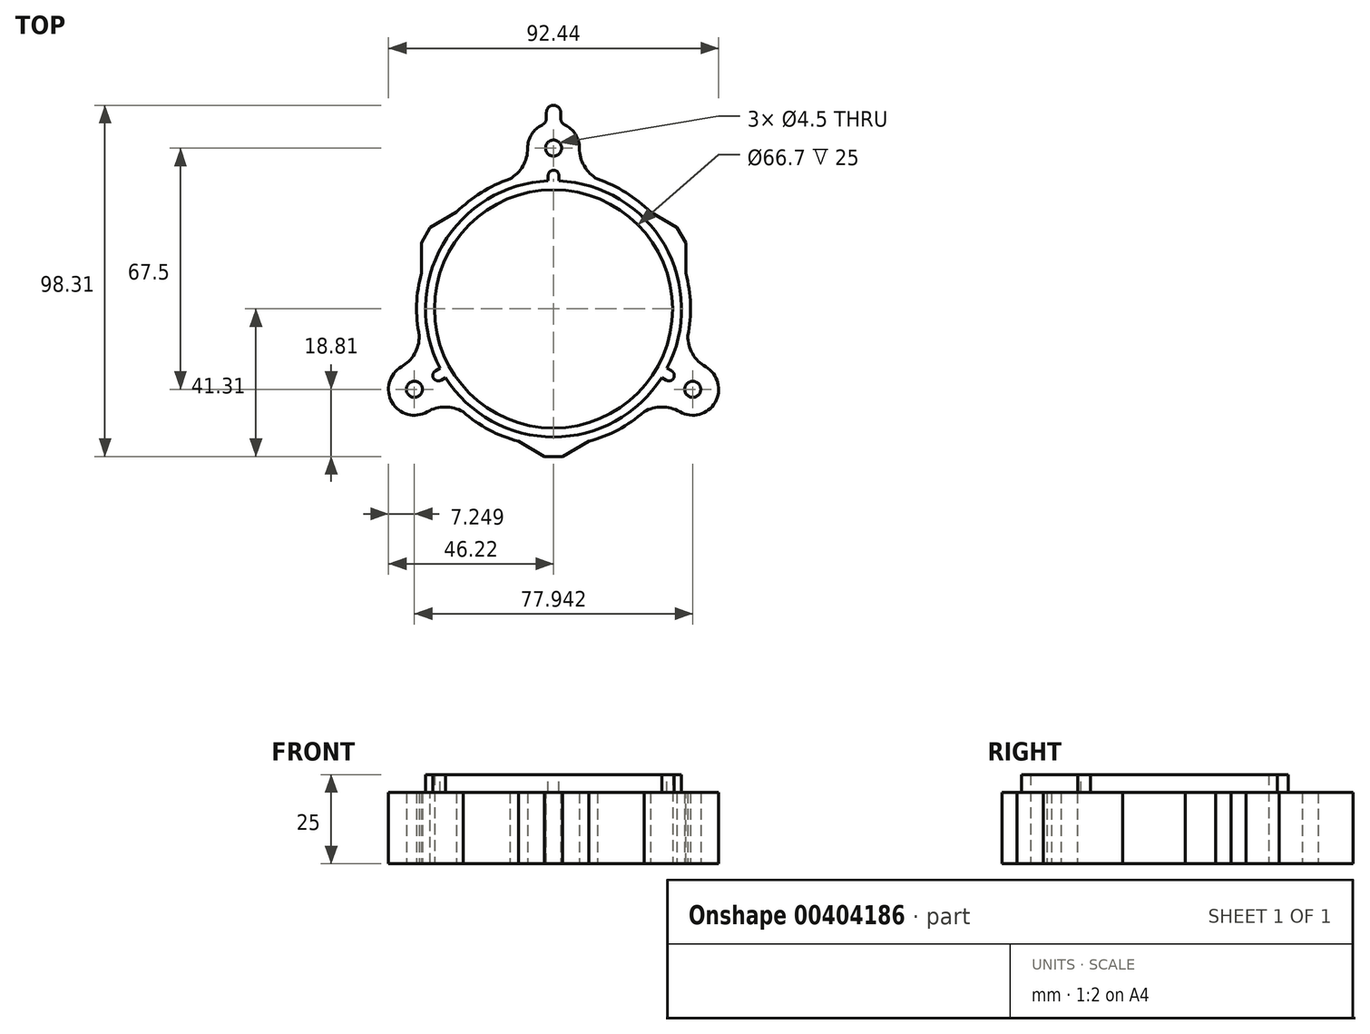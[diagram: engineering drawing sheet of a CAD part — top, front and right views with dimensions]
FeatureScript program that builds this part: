
annotation { "Feature Type Name" : "Feature", "Feature Type Description" : "" }
export const myFeature = defineFeature(function(context is Context, id is Id, definition is map)
    precondition{}
    {
        {
            var Q0;
            Q0=qCreatedBy(makeId("Top.planeOp"),FACE);
            var sketch = newSketch(context, id + "F0", { "sketchPlane" : qUnion([Q0])});
            skCircle(sketch, "E0", {"center": v(0, 0) * mm, "radius": 33.35 * mm});
            skCircle(sketch, "E1", {"center": v(0, 45) * mm, "radius": 2.25 * mm});
            skCircle(sketch, "E2", {"center": v(38.97, -22.5) * mm, "radius": 2.25 * mm});
            skCircle(sketch, "E3", {"center": v(-38.97, -22.5) * mm, "radius": 2.25 * mm});
            skArc(sketch, "E4", {"start": v(-25.35, -28.78) * mm, "mid": v(0, -38.35) * mm, "end": v(25.35, -28.78) * mm});
            skLineSegment(sketch, "E5", {"start": v(0, 0) * mm, "end": v(38.97, -22.5) * mm, "construction": true});
            skLineSegment(sketch, "E6", {"start": v(-38.97, -22.5) * mm, "end": v(0, 0) * mm, "construction": true});
            skArc(sketch, "E7", {"start": v(7.25, 45) * mm, "mid": v(5.8, 49.36) * mm, "end": v(2, 51.97) * mm});
            skArc(sketch, "E8.1.0", {"start": v(-42.6, -16.22) * mm, "mid": v(-45.25, -26.12) * mm, "end": v(-35.35, -28.78) * mm});
            skArc(sketch, "E8.2.0", {"start": v(35.35, -28.78) * mm, "mid": v(45.25, -26.12) * mm, "end": v(42.6, -16.22) * mm});
            skArc(sketch, "E9", {"start": v(-12.25, 36.34) * mm, "mid": v(-8.59, 40) * mm, "end": v(-7.25, 45) * mm});
            skArc(sketch, "E10.MirrorCS", {"start": v(12.25, 36.34) * mm, "mid": v(8.59, 40) * mm, "end": v(7.25, 45) * mm});
            skArc(sketch, "E11.1.0", {"start": v(-25.35, -28.78) * mm, "mid": v(-30.35, -27.44) * mm, "end": v(-35.35, -28.78) * mm});
            skArc(sketch, "E11.1.1", {"start": v(-37.6, -7.57) * mm, "mid": v(-38.94, -12.56) * mm, "end": v(-42.6, -16.22) * mm});
            skArc(sketch, "E11.2.0", {"start": v(37.6, -7.57) * mm, "mid": v(38.94, -12.56) * mm, "end": v(42.6, -16.22) * mm});
            skArc(sketch, "E11.2.1", {"start": v(25.35, -28.78) * mm, "mid": v(30.35, -27.44) * mm, "end": v(35.35, -28.78) * mm});
            skArc(sketch, "E12.trimOffspring", {"start": v(37.6, -7.57) * mm, "mid": v(33.21, 19.18) * mm, "end": v(12.25, 36.34) * mm});
            skArc(sketch, "E13.trimOffspring", {"start": v(-12.25, 36.34) * mm, "mid": v(-33.21, 19.17) * mm, "end": v(-37.6, -7.57) * mm});
            skLineSegment(sketch, "E14", {"start": v(-2, 54.13) * mm, "end": v(-2, 51.97) * mm});
            skArc(sketch, "E15", {"start": v(-2, 54.13) * mm, "mid": v(0, 60.5) * mm, "end": v(2, 54.13) * mm, "construction": true});
            skLineSegment(sketch, "E16.MirrorCS", {"start": v(2, 54.13) * mm, "end": v(2, 51.97) * mm});
            skArc(sketch, "E17.trimOffspring", {"start": v(-2, 51.97) * mm, "mid": v(-5.8, 49.36) * mm, "end": v(-7.25, 45) * mm});
            skLineSegment(sketch, "E18", {"start": v(0, 57) * mm, "end": v(-2, 57) * mm});
            skLineSegment(sketch, "E19", {"start": v(-2, 57) * mm, "end": v(-2, 54.13) * mm});
            skLineSegment(sketch, "E20.MirrorCS", {"start": v(0, 57) * mm, "end": v(2, 57) * mm});
            skLineSegment(sketch, "E21.MirrorCS", {"start": v(2, 57) * mm, "end": v(2, 54.13) * mm});
            skSolve(sketch);
        }
        {
            var Q0;
            Q0=qSketchRegion(id+"F0",true);
            extrude(context, id + "F1", {"entities" : qUnion([Q0]), "depth" : 20 * mm});
        }
        {
            var Q0;
            Q0=qCreatedBy(makeId("Top.planeOp"),FACE);
            var sketch = newSketch(context, id + "F2", { "sketchPlane" : qUnion([Q0])});
            skCircle(sketch, "E22.cCircle", {"center": v(0, 0) * mm, "radius": 37.02 * mm, "construction": true});
            skLineSegment(sketch, "E22.0", {"start": v(37.02, 21.37) * mm, "end": v(37.02, -21.37) * mm});
            skLineSegment(sketch, "E22.1", {"start": v(37.02, -21.37) * mm, "end": v(0, -42.75) * mm});
            skLineSegment(sketch, "E22.2", {"start": v(0, -42.75) * mm, "end": v(-37.02, -21.37) * mm});
            skLineSegment(sketch, "E22.3", {"start": v(-37.02, -21.37) * mm, "end": v(-37.02, 21.37) * mm});
            skLineSegment(sketch, "E22.4", {"start": v(-37.02, 21.37) * mm, "end": v(0, 42.75) * mm});
            skLineSegment(sketch, "E22.5", {"start": v(0, 42.75) * mm, "end": v(37.02, 21.38) * mm});
            skPoint(sketch, "E22.0.midPoint", {"position": v(37.02, 0) * mm});
            skCircle(sketch, "E23", {"center": v(0, 0) * mm, "radius": 33.35 * mm});
            skSolve(sketch);
        }
        {
            var Q0;
            Q0=qSketchRegion(id+"F2",true);
            extrude(context, id + "F3", {"entities" : qUnion([Q0]), "operationType" : NewBodyOperationType.ADD, "depth" : 25 * mm});
        }
        {
            var Q0;
            Q0=makeQuery(id+"F3.opExtrude","CAP_FACE",FACE,{"disambiguationData":[OSD([sQuery(id+"F2.wireOp",EDGE,"E22.0"),sQuery(id+"F2.wireOp",EDGE,"E22.1"),sQuery(id+"F2.wireOp",EDGE,"E22.2"),sQuery(id+"F2.wireOp",EDGE,"E22.3"),sQuery(id+"F2.wireOp",EDGE,"E22.4"),sQuery(id+"F2.wireOp",EDGE,"E22.5"),sQuery(id+"F2.wireOp",EDGE,"E23")])],"isStart":false});
            var sketch = newSketch(context, id + "F4", { "sketchPlane" : qUnion([Q0])});
            skArc(sketch, "E24", {"start": v(-1.5, 35.82) * mm, "mid": v(-31.05, 17.93) * mm, "end": v(-31.77, -16.61) * mm});
            skLineSegment(sketch, "E25", {"start": v(0, 38.82) * mm, "end": v(-1.5, 38.82) * mm});
            skLineSegment(sketch, "E26", {"start": v(-1.5, 38.82) * mm, "end": v(-1.5, 35.82) * mm});
            skLineSegment(sketch, "E27.MirrorCS", {"start": v(1.5, 38.82) * mm, "end": v(1.5, 35.82) * mm});
            skLineSegment(sketch, "E28.MirrorCS", {"start": v(0, 38.82) * mm, "end": v(1.5, 38.82) * mm});
            skLineSegment(sketch, "E29.1.0", {"start": v(-34.37, -18.11) * mm, "end": v(-31.77, -16.61) * mm});
            skLineSegment(sketch, "E29.1.1", {"start": v(-32.87, -20.7) * mm, "end": v(-30.27, -19.2) * mm});
            skLineSegment(sketch, "E29.1.2", {"start": v(-33.62, -19.4) * mm, "end": v(-32.87, -20.7) * mm});
            skLineSegment(sketch, "E29.1.3", {"start": v(-33.62, -19.4) * mm, "end": v(-34.37, -18.11) * mm});
            skLineSegment(sketch, "E29.2.0", {"start": v(32.87, -20.7) * mm, "end": v(30.27, -19.2) * mm});
            skLineSegment(sketch, "E29.2.1", {"start": v(34.37, -18.11) * mm, "end": v(31.77, -16.61) * mm});
            skLineSegment(sketch, "E29.2.2", {"start": v(33.62, -19.4) * mm, "end": v(34.37, -18.11) * mm});
            skLineSegment(sketch, "E29.2.3", {"start": v(33.62, -19.4) * mm, "end": v(32.87, -20.7) * mm});
            skArc(sketch, "E30.trimOffspring", {"start": v(31.77, -16.61) * mm, "mid": v(31.05, 17.93) * mm, "end": v(1.5, 35.82) * mm});
            skArc(sketch, "E31.trimOffspring", {"start": v(-30.27, -19.2) * mm, "mid": v(0, -35.85) * mm, "end": v(30.27, -19.2) * mm});
            skCircle(sketch, "E32.cCircle", {"center": v(0, 0) * mm, "radius": 37.02 * mm, "construction": true});
            skLineSegment(sketch, "E32.0", {"start": v(37.02, 21.37) * mm, "end": v(37.02, -21.37) * mm});
            skLineSegment(sketch, "E32.1", {"start": v(37.02, -21.38) * mm, "end": v(0, -42.75) * mm});
            skLineSegment(sketch, "E32.2", {"start": v(0, -42.75) * mm, "end": v(-37.02, -21.38) * mm});
            skLineSegment(sketch, "E32.3", {"start": v(-37.02, -21.38) * mm, "end": v(-37.02, 21.37) * mm});
            skLineSegment(sketch, "E32.4", {"start": v(-37.02, 21.37) * mm, "end": v(0, 42.75) * mm});
            skLineSegment(sketch, "E32.5", {"start": v(0, 42.75) * mm, "end": v(37.02, 21.37) * mm});
            skPoint(sketch, "E32.0.midPoint", {"position": v(37.02, 0) * mm});
            skSolve(sketch);
        }
        {
            var Q0;
            Q0=qSketchRegion(id+"F4",true);
            extrude(context, id + "F5", {"entities" : qUnion([Q0]), "operationType" : NewBodyOperationType.REMOVE, "oppositeDirection" : true, "depth" : 5 * mm});
        }
        {
            var Q0;
            Q0=makeQuery(id+"F5.boolean.opBoolean","COPY",EDGE,{"derivedFrom":makeQuery(id+"F5.opExtrude","SWEPT_EDGE",EDGE,{"disambiguationData":[OSD([sQuery(id+"F4.wireOp",EDGE,"E29.1.1"),sQuery(id+"F4.wireOp",EDGE,"E29.1.2")])]})});
            var Q1;
            Q1=makeQuery(id+"F5.boolean.opBoolean","COPY",EDGE,{"derivedFrom":makeQuery(id+"F5.opExtrude","SWEPT_EDGE",EDGE,{"disambiguationData":[OSD([sQuery(id+"F4.wireOp",EDGE,"E29.1.0"),sQuery(id+"F4.wireOp",EDGE,"E29.1.3")])]})});
            var Q2;
            Q2=makeQuery(id+"F5.boolean.opBoolean","COPY",EDGE,{"derivedFrom":makeQuery(id+"F5.opExtrude","SWEPT_EDGE",EDGE,{"disambiguationData":[OSD([sQuery(id+"F4.wireOp",EDGE,"E29.2.0"),sQuery(id+"F4.wireOp",EDGE,"E29.2.3")])]})});
            var Q3;
            Q3=makeQuery(id+"F5.boolean.opBoolean","COPY",EDGE,{"derivedFrom":makeQuery(id+"F5.opExtrude","SWEPT_EDGE",EDGE,{"disambiguationData":[OSD([sQuery(id+"F4.wireOp",EDGE,"E29.2.1"),sQuery(id+"F4.wireOp",EDGE,"E29.2.2")])]})});
            var Q4;
            Q4=makeQuery(id+"F5.boolean.opBoolean","COPY",EDGE,{"derivedFrom":makeQuery(id+"F5.opExtrude","SWEPT_EDGE",EDGE,{"disambiguationData":[OSD([sQuery(id+"F4.wireOp",EDGE,"E27.MirrorCS"),sQuery(id+"F4.wireOp",EDGE,"E28.MirrorCS")])]})});
            var Q5;
            Q5=makeQuery(id+"F5.boolean.opBoolean","COPY",EDGE,{"derivedFrom":makeQuery(id+"F5.opExtrude","SWEPT_EDGE",EDGE,{"disambiguationData":[OSD([sQuery(id+"F4.wireOp",EDGE,"E25"),sQuery(id+"F4.wireOp",EDGE,"E26")])]})});
            fillet(context, id + "F6", {"entities" : qUnion([Q0, Q1, Q2, Q3, Q4, Q5]), "radius" : 1.5 * mm, "tangentPropagation" : true, "allowEdgeOverflow" : false});
        }
        {
            var Q0;
            Q0=makeQuery(id+"F3.opExtrude","SWEPT_EDGE",EDGE,{"disambiguationData":[OSD([sQuery(id+"F2.wireOp",EDGE,"E22.1"),sQuery(id+"F2.wireOp",EDGE,"E22.2")])]});
            var Q1;
            Q1=makeQuery(id+"F3.opExtrude","SWEPT_EDGE",EDGE,{"disambiguationData":[OSD([sQuery(id+"F2.wireOp",EDGE,"E22.0"),sQuery(id+"F2.wireOp",EDGE,"E22.5")])]});
            var Q2;
            Q2=makeQuery(id+"F3.opExtrude","SWEPT_EDGE",EDGE,{"disambiguationData":[OSD([sQuery(id+"F2.wireOp",EDGE,"E22.3"),sQuery(id+"F2.wireOp",EDGE,"E22.4")])]});
            chamfer(context, id + "F7", {"entities" : qUnion([Q0, Q1, Q2]), "width" : 5 * mm, "tangentPropagation" : true});
        }
        {
            var Q0;
            Q0=makeQuery(id+"F1.opExtrude","SWEPT_EDGE",EDGE,{"disambiguationData":[OSD([sQuery(id+"F0.wireOp",EDGE,"E18"),sQuery(id+"F0.wireOp",EDGE,"E19")])]});
            var Q1;
            Q1=makeQuery(id+"F1.opExtrude","SWEPT_EDGE",EDGE,{"disambiguationData":[OSD([sQuery(id+"F0.wireOp",EDGE,"E20.MirrorCS"),sQuery(id+"F0.wireOp",EDGE,"E21.MirrorCS")])]});
            var Q2;
            Q2=makeQuery(id+"F1.opExtrude","SWEPT_EDGE",EDGE,{"disambiguationData":[OSD([sQuery(id+"F0.wireOp",EDGE,"E14"),sQuery(id+"F0.wireOp",EDGE,"E17.trimOffspring")])]});
            var Q3;
            Q3=makeQuery(id+"F1.opExtrude","SWEPT_EDGE",EDGE,{"disambiguationData":[OSD([sQuery(id+"F0.wireOp",EDGE,"E7"),sQuery(id+"F0.wireOp",EDGE,"E16.MirrorCS")])]});
            fillet(context, id + "F8", {"entities" : qUnion([Q0, Q1, Q2, Q3]), "radius" : 2 * mm, "tangentPropagation" : true, "allowEdgeOverflow" : false});
        }
    });
